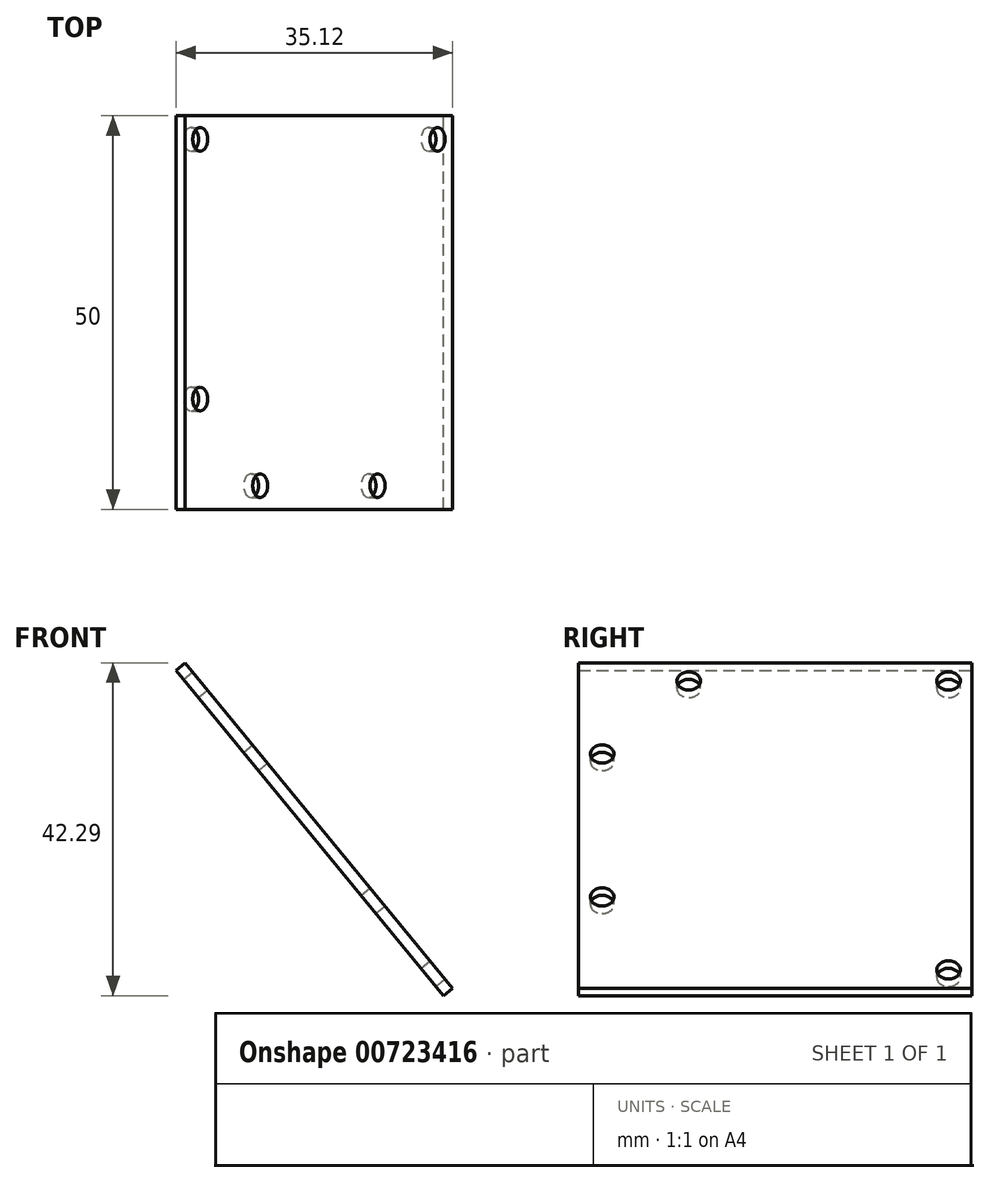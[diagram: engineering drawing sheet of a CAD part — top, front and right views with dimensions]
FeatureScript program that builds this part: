
annotation { "Feature Type Name" : "Feature", "Feature Type Description" : "" }
export const myFeature = defineFeature(function(context is Context, id is Id, definition is map)
    precondition{}
    {
        {
            var Q0;
            Q0=qCreatedBy(makeId("Front.planeOp"),FACE);
            var sketch = newSketch(context, id + "F0", { "sketchPlane" : qUnion([Q0])});
            skLineSegment(sketch, "E0", {"start": v(-36.92, 88.45) * mm, "end": v(-36.92, -12.33) * mm});
            skLineSegment(sketch, "E1", {"start": v(-36.92, 63.05) * mm, "end": v(-2.96, 21.7) * mm});
            skLineSegment(sketch, "E2", {"start": v(-2.96, 21.7) * mm, "end": v(-36.92, 21.7) * mm, "construction": true});
            skSolve(sketch);
        }
        {
            var Q0;
            Q0=sQuery(id+"F0.wireOp",EDGE,"E1");
            extrude(context, id + "F1", {"bodyType" : ToolBodyType.SURFACE, "surfaceEntities" : qUnion([Q0]), "oppositeDirection" : true, "depth" : 50 * mm, "offsetDistance" : 25 * mm});
        }
        {
            var Q0;
            Q0=makeQuery(id+"F1.opExtrude","SWEPT_FACE",FACE,{"disambiguationData":[OSD([sQuery(id+"F0.wireOp",EDGE,"E1")])]});
            extrude(context, id + "F2", {"entities" : qUnion([Q0]), "depth" : 1.5 * mm, "offsetDistance" : 25 * mm});
        }
        {
            var Q0;
            Q0=makeQuery(id+"F2.opExtrude","CAP_FACE",FACE,{"disambiguationData":[OSD([sQuery(id+"F0.wireOp",EDGE,"E1")])],"isStart":false});
            var sketch = newSketch(context, id + "F3", { "sketchPlane" : qUnion([Q0])});
            skLineSegment(sketch, "E3", {"start": v(0, 69.16) * mm, "end": v(50, 69.16) * mm, "construction": true});
            skLineSegment(sketch, "E4", {"start": v(47, 72.16) * mm, "end": v(47, 18.66) * mm, "construction": true});
            skLineSegment(sketch, "E5", {"start": v(0, 21.66) * mm, "end": v(50, 21.66) * mm, "construction": true});
            skCircle(sketch, "E6", {"center": v(47, 69.16) * mm, "radius": 1.5 * mm});
            skCircle(sketch, "E7", {"center": v(47, 21.66) * mm, "radius": 1.5 * mm});
            skLineSegment(sketch, "E8", {"start": v(6, 72.16) * mm, "end": v(6, 18.66) * mm, "construction": true});
            skLineSegment(sketch, "E9", {"start": v(0, 60.16) * mm, "end": v(50, 60.16) * mm, "construction": true});
            skLineSegment(sketch, "E10", {"start": v(0, 30.66) * mm, "end": v(50, 30.66) * mm, "construction": true});
            skLineSegment(sketch, "E11", {"start": v(3, 72.16) * mm, "end": v(3, 18.66) * mm, "construction": true});
            skLineSegment(sketch, "E12", {"start": v(0, 57.16) * mm, "end": v(50, 57.16) * mm, "construction": true});
            skLineSegment(sketch, "E13", {"start": v(0, 33.66) * mm, "end": v(50, 33.66) * mm, "construction": true});
            skCircle(sketch, "E14", {"center": v(3, 33.66) * mm, "radius": 1.5 * mm});
            skCircle(sketch, "E15", {"center": v(3, 57.16) * mm, "radius": 1.5 * mm});
            skLineSegment(sketch, "E16", {"start": v(14, 72.16) * mm, "end": v(14, 18.66) * mm, "construction": true});
            skCircle(sketch, "E17", {"center": v(14, 69.16) * mm, "radius": 1.5 * mm});
            skSolve(sketch);
        }
        {
            var Q0;
            Q0=makeQuery(id+"F3.imprint","IMPRINT",FACE,{"disambiguationData":[TD([[makeQuery(id+"F3.imprint","IMPRINT",EDGE,{"derivedFrom":sQuery(id+"F3.wireOp",EDGE,"E15")}),1.0]])]});
            var Q1;
            Q1=makeQuery(id+"F3.imprint","IMPRINT",FACE,{"disambiguationData":[TD([[makeQuery(id+"F3.imprint","IMPRINT",EDGE,{"derivedFrom":sQuery(id+"F3.wireOp",EDGE,"E14")}),1.0]])]});
            var Q2;
            Q2=makeQuery(id+"F3.imprint","IMPRINT",FACE,{"disambiguationData":[TD([[makeQuery(id+"F3.imprint","IMPRINT",EDGE,{"derivedFrom":sQuery(id+"F3.wireOp",EDGE,"E6")}),1.0]])]});
            var Q3;
            Q3=makeQuery(id+"F3.imprint","IMPRINT",FACE,{"disambiguationData":[TD([[makeQuery(id+"F3.imprint","IMPRINT",EDGE,{"derivedFrom":sQuery(id+"F3.wireOp",EDGE,"E7")}),1.0]])]});
            var Q4;
            Q4=makeQuery(id+"F3.imprint","IMPRINT",FACE,{"disambiguationData":[TD([[makeQuery(id+"F3.imprint","IMPRINT",EDGE,{"derivedFrom":sQuery(id+"F3.wireOp",EDGE,"E17")}),1.0]])]});
            extrude(context, id + "F4", {"entities" : qUnion([Q0, Q1, Q2, Q3, Q4]), "operationType" : NewBodyOperationType.REMOVE, "oppositeDirection" : true, "depth" : 25 * mm, "offsetDistance" : 25 * mm});
        }
    });
